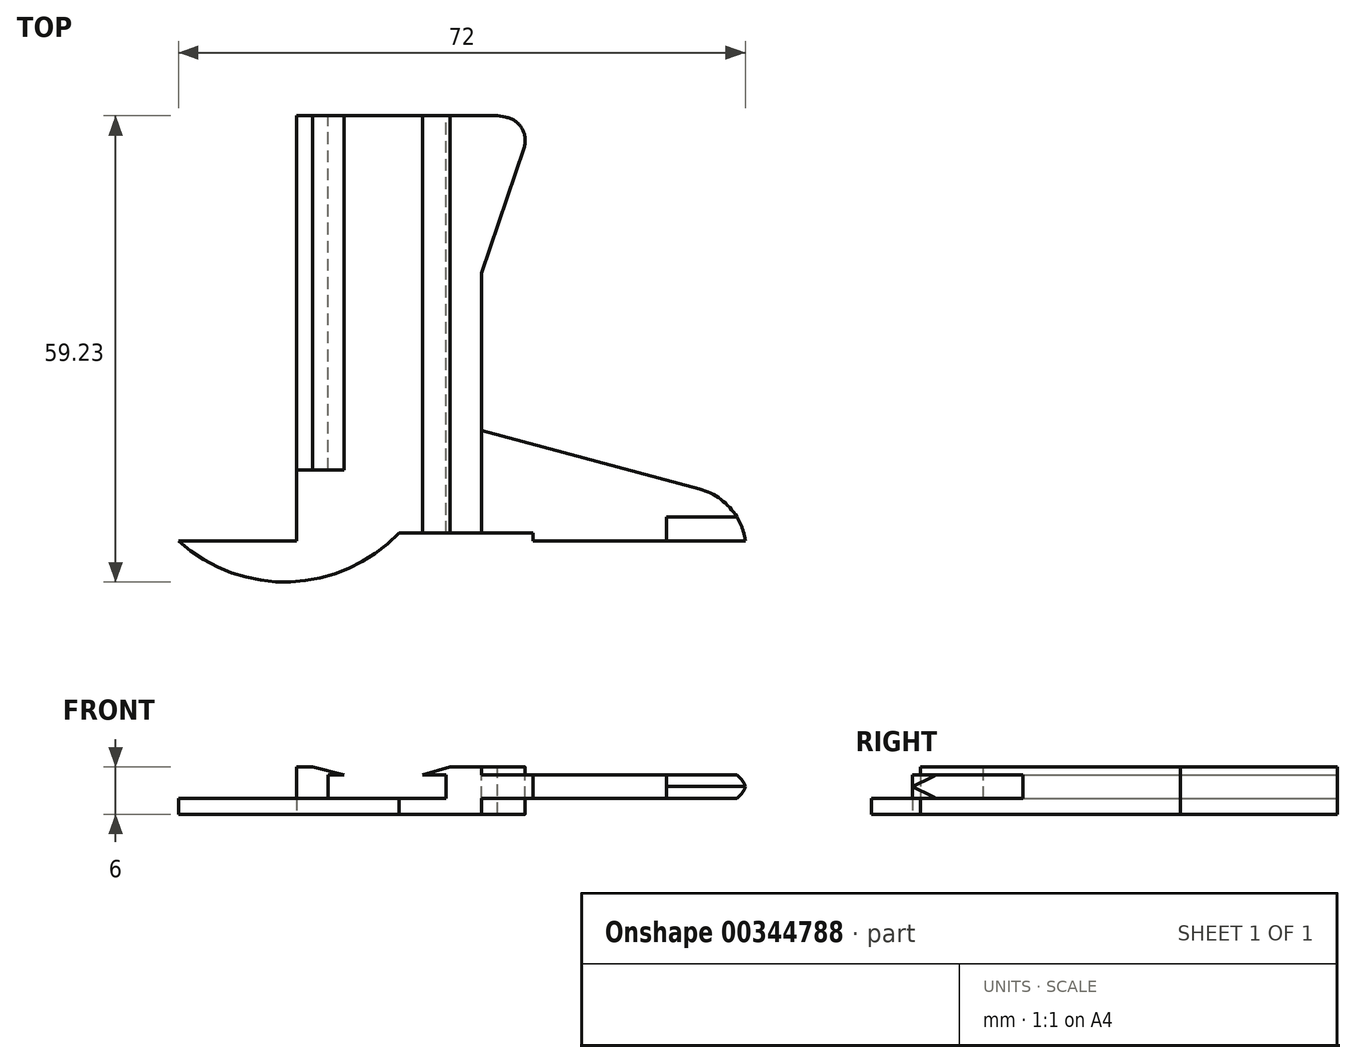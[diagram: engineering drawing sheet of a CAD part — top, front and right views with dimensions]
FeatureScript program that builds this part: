
annotation { "Feature Type Name" : "Feature", "Feature Type Description" : "" }
export const myFeature = defineFeature(function(context is Context, id is Id, definition is map)
    precondition{}
    {
        {
            var Q0;
            Q0=qCreatedBy(makeId("Front.planeOp"),FACE);
            var sketch = newSketch(context, id + "F0", { "sketchPlane" : qUnion([Q0])});
            skLineSegment(sketch, "E0", {"start": v(0, 0) * mm, "end": v(-15, 0) * mm});
            skLineSegment(sketch, "E1", {"start": v(-15, 0) * mm, "end": v(-15, 3) * mm});
            skLineSegment(sketch, "E2", {"start": v(-15, 3) * mm, "end": v(-13, 3) * mm});
            skLineSegment(sketch, "E3", {"start": v(-13, 3) * mm, "end": v(-17, 4) * mm});
            skLineSegment(sketch, "E4", {"start": v(-17, 4) * mm, "end": v(-19, 4) * mm});
            skLineSegment(sketch, "E5", {"start": v(-19, 4) * mm, "end": v(-19, -2) * mm});
            skLineSegment(sketch, "E6", {"start": v(-19, -2) * mm, "end": v(4.5, -2) * mm});
            skLineSegment(sketch, "E7", {"start": v(4.5, -2) * mm, "end": v(4.5, 4) * mm});
            skLineSegment(sketch, "E8", {"start": v(4.5, 4) * mm, "end": v(0.5, 4) * mm});
            skLineSegment(sketch, "E9", {"start": v(0.5, 4) * mm, "end": v(-3, 3) * mm});
            skLineSegment(sketch, "E10", {"start": v(-3, 3) * mm, "end": v(0, 3) * mm});
            skLineSegment(sketch, "E11", {"start": v(0, 3) * mm, "end": v(0, 0) * mm});
            skSolve(sketch);
        }
        {
            var Q0;
            Q0=makeQuery(id+"F0.imprint","IMPRINT",FACE,{"disambiguationData":[TD([[makeQuery(id+"F0.imprint","IMPRINT",EDGE,{"derivedFrom":sQuery(id+"F0.wireOp",EDGE,"E0")}),1.0]])]});
            extrude(context, id + "F1", {"entities" : qUnion([Q0]), "depth" : 53 * mm});
        }
        {
            var Q0;
            Q0=qCreatedBy(makeId("Top.planeOp"),FACE);
            var sketch = newSketch(context, id + "F2", { "sketchPlane" : qUnion([Q0])});
            skLineSegment(sketch, "E12", {"start": v(4.5, -40) * mm, "end": v(32.15, -47.4) * mm});
            skLineSegment(sketch, "E13", {"start": v(38, -54) * mm, "end": v(11, -54) * mm});
            skLineSegment(sketch, "E14", {"start": v(11, -54) * mm, "end": v(11, -53) * mm});
            skLineSegment(sketch, "E15", {"start": v(11, -53) * mm, "end": v(4.5, -53) * mm});
            skLineSegment(sketch, "E16.0", {"start": v(4.5, -53) * mm, "end": v(4.5, 0) * mm});
            skArc(sketch, "E17", {"start": v(38, -54) * mm, "mid": v(36.07, -49.83) * mm, "end": v(32.15, -47.4) * mm});
            skSolve(sketch);
        }
        {
            var Q0;
            {var subQ1=sQuery(id+"F2.wireOp",EDGE,"E12");Q0=makeQuery(id+"F2.imprint","IMPRINT",FACE,{"disambiguationData":[TD([[makeQuery(id+"F2.imprint","IMPRINT",EDGE,{"derivedFrom":subQ1}),-1.0]])]});}
            extrude(context, id + "F3", {"entities" : qUnion([Q0]), "operationType" : NewBodyOperationType.ADD, "depth" : 3 * mm});
        }
        {
            var Q0;
            Q0=qCreatedBy(makeId("Right.planeOp"),FACE);
            cPlane(context, id + "F4", {"entities" : qUnion([Q0]), "cplaneType" : CPlaneType.OFFSET, "offset" : 38 * mm, "width" : 150 * mm, "height" : 150 * mm});
        }
        {
            var Q0;
            Q0=qCreatedBy(id+"F4.planeOp",FACE);
            var sketch = newSketch(context, id + "F5", { "sketchPlane" : qUnion([Q0])});
            skLineSegment(sketch, "E18", {"start": v(-59, 0) * mm, "end": v(-51, 0) * mm});
            skLineSegment(sketch, "E19", {"start": v(-51, 0) * mm, "end": v(-54, 1.5) * mm});
            skLineSegment(sketch, "E20", {"start": v(-54, 1.5) * mm, "end": v(-51, 3) * mm});
            skLineSegment(sketch, "E21", {"start": v(-51, 3) * mm, "end": v(-59, 3) * mm});
            skLineSegment(sketch, "E22", {"start": v(-59, 3) * mm, "end": v(-59, 0) * mm});
            skSolve(sketch);
        }
        {
            var Q0;
            Q0=makeQuery(id+"F5.imprint","IMPRINT",FACE,{"disambiguationData":[TD([[makeQuery(id+"F5.imprint","IMPRINT",EDGE,{"derivedFrom":sQuery(id+"F5.wireOp",EDGE,"E18")}),1.0]])]});
            extrude(context, id + "F6", {"entities" : qUnion([Q0]), "operationType" : NewBodyOperationType.REMOVE, "oppositeDirection" : true, "depth" : 10 * mm});
        }
        {
            var Q0;
            Q0=makeQuery(id+"F1.opExtrude","SWEPT_FACE",FACE,{"disambiguationData":[OSD([sQuery(id+"F0.wireOp",EDGE,"E6")])]});
            var sketch = newSketch(context, id + "F7", { "sketchPlane" : qUnion([Q0])});
            skLineSegment(sketch, "E23.0", {"start": v(-19, 53) * mm, "end": v(-19, 0) * mm});
            skLineSegment(sketch, "E24.0.0", {"start": v(-19, 0) * mm, "end": v(4.5, 0) * mm});
            skLineSegment(sketch, "E24.0.1", {"start": v(4.5, 0) * mm, "end": v(4.5, 53) * mm});
            skLineSegment(sketch, "E24.0.2", {"start": v(4.5, 53) * mm, "end": v(-19, 53) * mm});
            skArc(sketch, "E25", {"start": v(-6, 53) * mm, "mid": v(-19.8, 59.22) * mm, "end": v(-34, 54) * mm});
            skLineSegment(sketch, "E26", {"start": v(-19, 53) * mm, "end": v(-19, 54) * mm});
            skLineSegment(sketch, "E27", {"start": v(-19, 54) * mm, "end": v(-34, 54) * mm});
            skSolve(sketch);
        }
        {
            var Q0;
            {var subQ2=sQuery(id+"F7.wireOp",EDGE,"E25");Q0=makeQuery(id+"F7.imprint","IMPRINT",FACE,{"disambiguationData":[TD([[makeQuery(id+"F7.imprint","IMPRINT",EDGE,{"derivedFrom":subQ2}),1.0]])]});}
            extrude(context, id + "F8", {"entities" : qUnion([Q0]), "operationType" : NewBodyOperationType.ADD, "oppositeDirection" : true, "depth" : 2 * mm});
        }
        {
            var Q0;
            Q0=makeQuery(id+"F1.opExtrude","SWEPT_FACE",FACE,{"disambiguationData":[OSD([sQuery(id+"F0.wireOp",EDGE,"E4")])]});
            var sketch = newSketch(context, id + "F9", { "sketchPlane" : qUnion([Q0])});
            skLineSegment(sketch, "E28.bottom", {"start": v(-19, -53) * mm, "end": v(-13, -53) * mm});
            skLineSegment(sketch, "E28.top", {"start": v(-19, -45) * mm, "end": v(-13, -45) * mm});
            skLineSegment(sketch, "E28.left", {"start": v(-19, -53) * mm, "end": v(-19, -45) * mm});
            skLineSegment(sketch, "E28.right", {"start": v(-13, -53) * mm, "end": v(-13, -45) * mm});
            skSolve(sketch);
        }
        {
            var Q0;
            {var subQ3=sQuery(id+"F9.wireOp",EDGE,"E28.right");Q0=makeQuery(id+"F9.imprint","IMPRINT",FACE,{"disambiguationData":[TD([[makeQuery(id+"F9.imprint","IMPRINT",EDGE,{"derivedFrom":subQ3}),1.0]])]});}
            var Q1;
            {var subQ4=sQuery(id+"F9.wireOp",EDGE,"E28.left");Q1=makeQuery(id+"F9.imprint","IMPRINT",FACE,{"disambiguationData":[TD([[makeQuery(id+"F9.imprint","IMPRINT",EDGE,{"derivedFrom":subQ4}),-1.0]])]});}
            extrude(context, id + "F10", {"entities" : qUnion([Q0, Q1]), "operationType" : NewBodyOperationType.REMOVE, "oppositeDirection" : true, "depth" : 4 * mm});
        }
        {
            var Q0;
            Q0=makeQuery(id+"F1.opExtrude","SWEPT_FACE",FACE,{"disambiguationData":[OSD([sQuery(id+"F0.wireOp",EDGE,"E8")])]});
            var sketch = newSketch(context, id + "F11", { "sketchPlane" : qUnion([Q0])});
            skLineSegment(sketch, "E29", {"start": v(4.5, -20) * mm, "end": v(11, -0.8) * mm});
            skLineSegment(sketch, "E30", {"start": v(11, -0.8) * mm, "end": v(6.5, 0) * mm});
            skLineSegment(sketch, "E31", {"start": v(6.5, 0) * mm, "end": v(4.5, 0) * mm});
            skLineSegment(sketch, "E32", {"start": v(4.5, 0) * mm, "end": v(4.5, -20) * mm});
            skSolve(sketch);
        }
        {
            var Q0;
            Q0=makeQuery(id+"F11.imprint","IMPRINT",FACE,{"disambiguationData":[TD([[makeQuery(id+"F11.imprint","IMPRINT",EDGE,{"derivedFrom":sQuery(id+"F11.wireOp",EDGE,"E29")}),1.0]])]});
            extrude(context, id + "F12", {"entities" : qUnion([Q0]), "operationType" : NewBodyOperationType.ADD, "oppositeDirection" : true, "depth" : 6 * mm});
        }
        {
            var Q0;
            Q0=makeQuery(id+"F12.opExtrude","SWEPT_EDGE",EDGE,{"disambiguationData":[OSD([sQuery(id+"F11.wireOp",EDGE,"E29"),sQuery(id+"F11.wireOp",EDGE,"E30")])]});
            fillet(context, id + "F13", {"entities" : qUnion([Q0]), "radius" : 3 * mm, "tangentPropagation" : true, "allowEdgeOverflow" : false});
        }
    });
